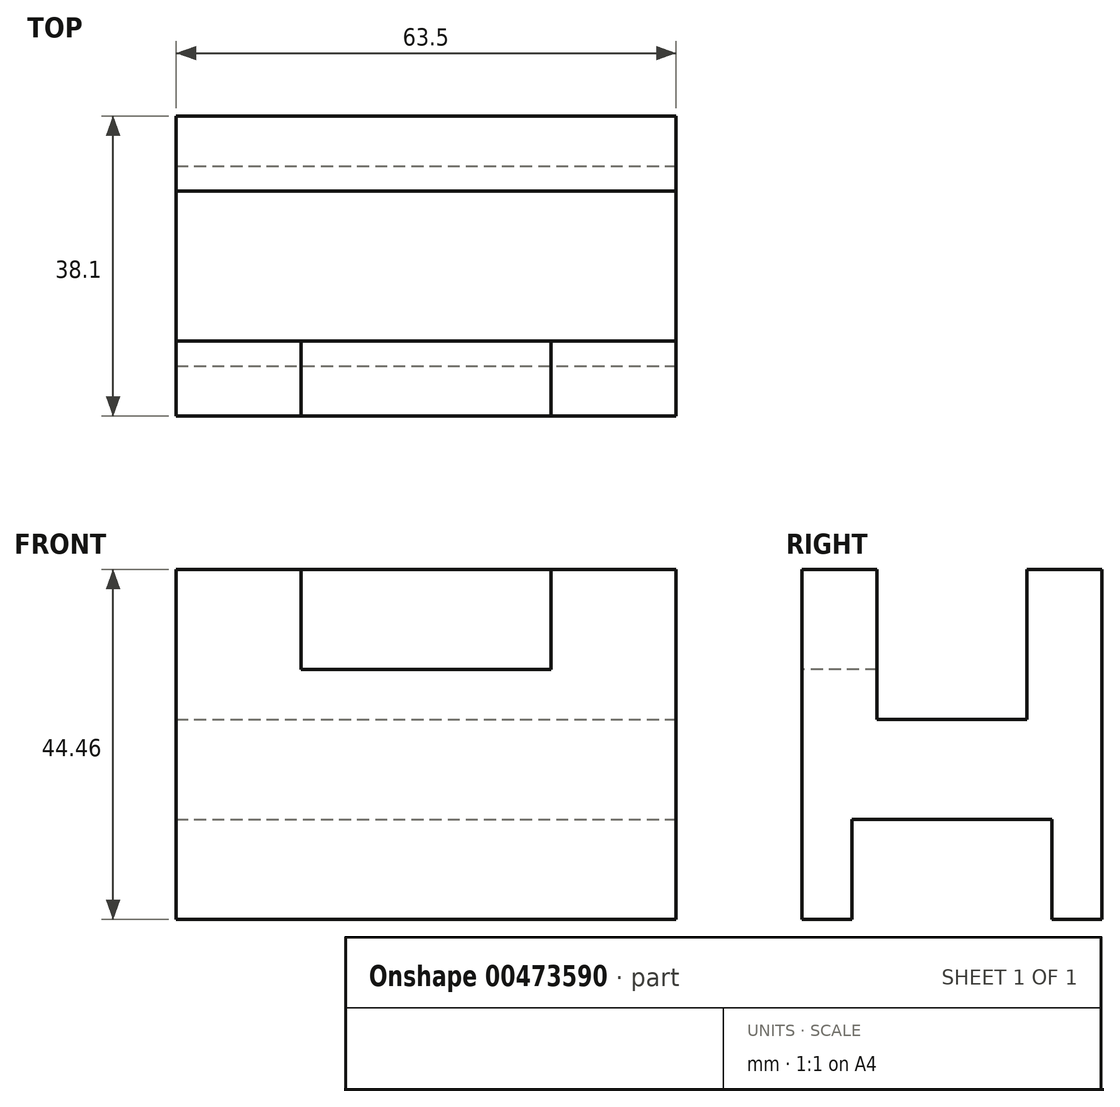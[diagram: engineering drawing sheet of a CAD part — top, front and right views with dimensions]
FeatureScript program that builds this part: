
annotation { "Feature Type Name" : "Feature", "Feature Type Description" : "" }
export const myFeature = defineFeature(function(context is Context, id is Id, definition is map)
    precondition{}
    {
        {
            var Q0;
            Q0=qCreatedBy(makeId("Front.planeOp"),FACE);
            var sketch = newSketch(context, id + "F0", { "sketchPlane" : qUnion([Q0])});
            skLineSegment(sketch, "E0.bottom", {"start": v(31.75, 22.23) * mm, "end": v(-31.75, 22.23) * mm});
            skLineSegment(sketch, "E0.top", {"start": v(31.75, -22.23) * mm, "end": v(-31.75, -22.23) * mm});
            skLineSegment(sketch, "E0.left", {"start": v(31.75, 22.23) * mm, "end": v(31.75, -22.23) * mm});
            skLineSegment(sketch, "E0.right", {"start": v(-31.75, 22.23) * mm, "end": v(-31.75, -22.23) * mm});
            skPoint(sketch, "E0.middle", {"position": v(0, 0) * mm});
            skSolve(sketch);
        }
        {
            var Q0;
            Q0=makeQuery(id+"F0.imprint","IMPRINT",FACE,{"disambiguationData":[TD([[makeQuery(id+"F0.imprint","IMPRINT",EDGE,{"derivedFrom":sQuery(id+"F0.wireOp",EDGE,"E0.bottom")}),1.0]])]});
            extrude(context, id + "F1", {"entities" : qUnion([Q0]), "depth" : 38.1 * mm});
        }
        {
            var Q0;
            Q0=makeQuery(id+"F1.opExtrude","SWEPT_FACE",FACE,{"disambiguationData":[OSD([sQuery(id+"F0.wireOp",EDGE,"E0.left")])]});
            var sketch = newSketch(context, id + "F2", { "sketchPlane" : qUnion([Q0])});
            skLineSegment(sketch, "E1.bottom", {"start": v(-31.75, -22.22) * mm, "end": v(-6.35, -22.22) * mm});
            skLineSegment(sketch, "E1.top", {"start": v(-31.75, -9.52) * mm, "end": v(-6.35, -9.52) * mm});
            skLineSegment(sketch, "E1.left", {"start": v(-31.75, -22.22) * mm, "end": v(-31.75, -9.52) * mm});
            skLineSegment(sketch, "E1.right", {"start": v(-6.35, -22.22) * mm, "end": v(-6.35, -9.52) * mm});
            skSolve(sketch);
        }
        {
            var Q0;
            Q0=makeQuery(id+"F2.imprint","IMPRINT",FACE,{"disambiguationData":[TD([[makeQuery(id+"F2.imprint","IMPRINT",EDGE,{"derivedFrom":sQuery(id+"F2.wireOp",EDGE,"E1.bottom")}),1.0]])]});
            extrude(context, id + "F3", {"entities" : qUnion([Q0]), "operationType" : NewBodyOperationType.REMOVE, "endBound" : BoundingType.THROUGH_ALL, "oppositeDirection" : true, "depth" : 38.1 * mm});
        }
        {
            var Q0;
            Q0=makeQuery(id+"F1.opExtrude","SWEPT_FACE",FACE,{"disambiguationData":[OSD([sQuery(id+"F0.wireOp",EDGE,"E0.left")])]});
            var sketch = newSketch(context, id + "F4", { "sketchPlane" : qUnion([Q0])});
            skLineSegment(sketch, "E2.bottom", {"start": v(-28.58, 22.23) * mm, "end": v(-9.53, 22.23) * mm});
            skLineSegment(sketch, "E2.top", {"start": v(-28.57, 3.18) * mm, "end": v(-9.52, 3.18) * mm});
            skLineSegment(sketch, "E2.left", {"start": v(-28.58, 22.23) * mm, "end": v(-28.58, 3.18) * mm});
            skLineSegment(sketch, "E2.right", {"start": v(-9.53, 22.23) * mm, "end": v(-9.53, 3.18) * mm});
            skSolve(sketch);
        }
        {
            var Q0;
            Q0=makeQuery(id+"F4.imprint","IMPRINT",FACE,{"disambiguationData":[TD([[makeQuery(id+"F4.imprint","IMPRINT",EDGE,{"derivedFrom":sQuery(id+"F4.wireOp",EDGE,"E2.bottom")}),-1.0]])]});
            extrude(context, id + "F5", {"entities" : qUnion([Q0]), "operationType" : NewBodyOperationType.REMOVE, "endBound" : BoundingType.THROUGH_ALL, "oppositeDirection" : true, "depth" : 25.4 * mm});
        }
        {
            var Q0;
            Q0=makeQuery(id+"F1.opExtrude","CAP_FACE",FACE,{"disambiguationData":[OSD([sQuery(id+"F0.wireOp",EDGE,"E0.bottom"),sQuery(id+"F0.wireOp",EDGE,"E0.top"),sQuery(id+"F0.wireOp",EDGE,"E0.left"),sQuery(id+"F0.wireOp",EDGE,"E0.right")])],"isStart":false});
            var sketch = newSketch(context, id + "F6", { "sketchPlane" : qUnion([Q0])});
            skLineSegment(sketch, "E3.bottom", {"start": v(-15.88, 22.23) * mm, "end": v(15.88, 22.23) * mm});
            skLineSegment(sketch, "E3.top", {"start": v(-15.88, 9.52) * mm, "end": v(15.88, 9.52) * mm});
            skLineSegment(sketch, "E3.left", {"start": v(-15.88, 22.23) * mm, "end": v(-15.88, 9.53) * mm});
            skLineSegment(sketch, "E3.right", {"start": v(15.88, 22.23) * mm, "end": v(15.88, 9.53) * mm});
            skSolve(sketch);
        }
        {
            var Q0;
            Q0=makeQuery(id+"F6.imprint","IMPRINT",FACE,{"disambiguationData":[TD([[makeQuery(id+"F6.imprint","IMPRINT",EDGE,{"derivedFrom":sQuery(id+"F6.wireOp",EDGE,"E3.bottom")}),1.0]])]});
            extrude(context, id + "F7", {"entities" : qUnion([Q0]), "operationType" : NewBodyOperationType.REMOVE, "oppositeDirection" : true, "depth" : 12.7 * mm});
        }
    });
